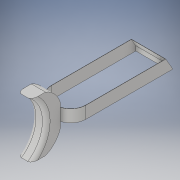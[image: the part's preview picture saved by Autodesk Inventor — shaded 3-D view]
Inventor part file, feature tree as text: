
AUTODESK INVENTOR PART (.ipt)
format: ipt  version: 2018.3 (Build 223284000, 284)  size: 205,312 bytes
history: native  units: in
note: dims shown in document units (in); Inventor stores cm internally (conversion verified against a paired STEP export)
features: sketch x5, extrude x4, plane x2, chamfer x1, mirror x1, thicken_offset x1, fillet x1
ambient origin geometry x8: Origin, YZ Plane, XZ Plane, XY Plane, X Axis, Y Axis, Z Axis, Center Point
bodies: Solid1 (feature_tree)
feature tree (15):
  sketch  "Sketch2"  dims[d1=2.052in d2=15.0deg]
  extrude  "Extrusion1"  TaperAngle=15.0deg  [1 undecoded]
  chamfer  "Chamfer1"  Distance=0.033in
  plane  "Work Plane1"
  extrude  "Extrusion2"  Depth=0.0625in
  mirror  "Mirror1"
  thicken_offset  "Thicken1"
  plane  "Work Plane3"
  extrude  "Extrusion3"  Depth=0.0625in
  extrude  "Extrusion4"  Depth=0.0625in TaperAngle=0.0deg
  fillet  "Fillet1"  Radius=0.1875in
  sketch  "Sketch3"  dims[d3=0.199in]
  sketch  "Sketch4"  dims[d4=1.655in]
  sketch  "Sketch6"  dims[d5=0.2775in]
  sketch  "Sketch8"  dims[d6=0.2815in d7=0.033in d9=0.0033in d10=1.6552in d11=0.199in d12=0.0in d13=0.1875in d14=0.1875in d15=30.0deg d16=0.0in d17=0.003in d18=0.0in d19=0.0058in d20=0.0058in d23=-0.3125in d24=1.0in d25=0.0in d27=0.357in d28=0.9in d29=0.413in d30=0.413in d31=0.47in d32=0.24in d33=0.23in d34=0.0in d35=0.0625in]
note: 1 required parameter value undecoded (feature->parameter linkage not recoverable at this tier; creation-order binding heuristic only, values carry confidence <= 0.55)
